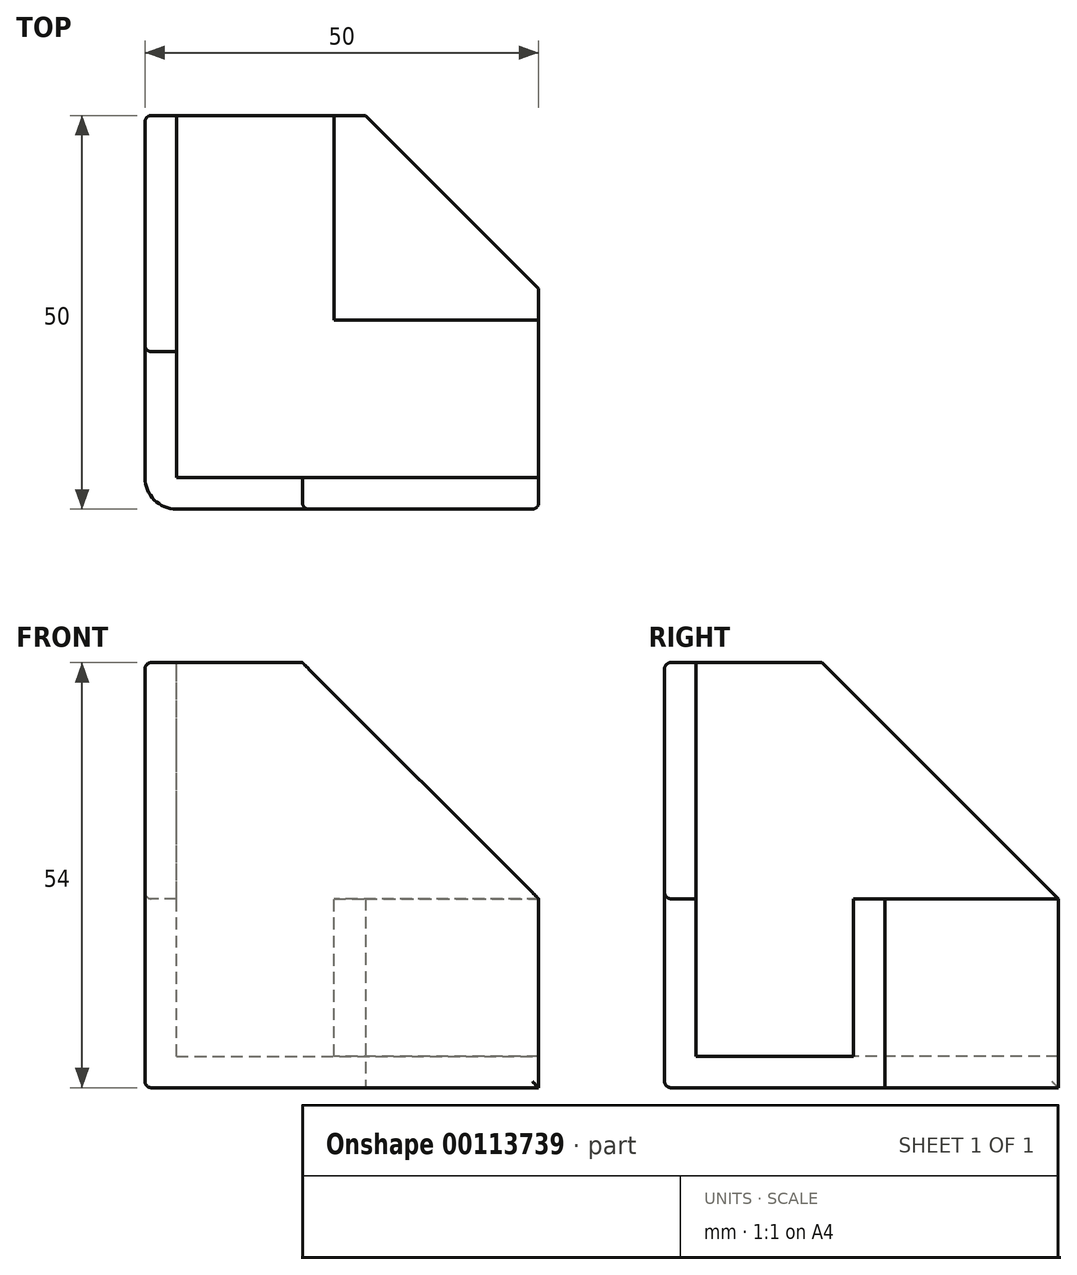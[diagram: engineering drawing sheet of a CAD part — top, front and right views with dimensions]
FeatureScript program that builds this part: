
annotation { "Feature Type Name" : "Feature", "Feature Type Description" : "" }
export const myFeature = defineFeature(function(context is Context, id is Id, definition is map)
    precondition{}
    {
        {
            var Q0;
            Q0=qCreatedBy(makeId("Top.planeOp"),FACE);
            var sketch = newSketch(context, id + "F0", { "sketchPlane" : qUnion([Q0])});
            skLineSegment(sketch, "E0", {"start": v(-64, 35.12) * mm, "end": v(-36, 35.12) * mm});
            skLineSegment(sketch, "E1", {"start": v(-36, 35.12) * mm, "end": v(-14, 13.12) * mm});
            skLineSegment(sketch, "E2", {"start": v(-14, 13.12) * mm, "end": v(-14, -14.88) * mm});
            skLineSegment(sketch, "E3", {"start": v(-14, -14.88) * mm, "end": v(-64, -14.88) * mm});
            skLineSegment(sketch, "E4", {"start": v(-64, -14.88) * mm, "end": v(-64, 35.12) * mm});
            skSolve(sketch);
        }
        {
            var Q0;
            Q0=makeQuery(id+"F0.imprint","IMPRINT",FACE,{"disambiguationData":[TD([[makeQuery(id+"F0.imprint","IMPRINT",EDGE,{"derivedFrom":sQuery(id+"F0.wireOp",EDGE,"E0")}),-1.0]])]});
            extrude(context, id + "F1", {"entities" : qUnion([Q0]), "depth" : 24 * mm});
        }
        {
            var Q0;
            Q0=makeQuery(id+"F1.opExtrude","CAP_FACE",FACE,{"disambiguationData":[OSD([sQuery(id+"F0.wireOp",EDGE,"E0"),sQuery(id+"F0.wireOp",EDGE,"E1"),sQuery(id+"F0.wireOp",EDGE,"E2"),sQuery(id+"F0.wireOp",EDGE,"E3"),sQuery(id+"F0.wireOp",EDGE,"E4")])],"isStart":false});
            var sketch = newSketch(context, id + "F2", { "sketchPlane" : qUnion([Q0])});
            skLineSegment(sketch, "E5", {"start": v(-60, 35.12) * mm, "end": v(-60, -10.88) * mm});
            skLineSegment(sketch, "E6", {"start": v(-60, -10.88) * mm, "end": v(-14, -10.88) * mm});
            skLineSegment(sketch, "E7", {"start": v(-14, -10.88) * mm, "end": v(-14, 9.12) * mm});
            skLineSegment(sketch, "E8", {"start": v(-14, 9.12) * mm, "end": v(-40, 9.12) * mm});
            skLineSegment(sketch, "E9", {"start": v(-40, 9.12) * mm, "end": v(-40, 35.12) * mm});
            skLineSegment(sketch, "E10", {"start": v(-40, 35.12) * mm, "end": v(-60, 35.12) * mm});
            skSolve(sketch);
        }
        {
            var Q0;
            Q0=makeQuery(id+"F2.imprint","IMPRINT",FACE,{"disambiguationData":[TD([[makeQuery(id+"F2.imprint","IMPRINT",EDGE,{"derivedFrom":sQuery(id+"F2.wireOp",EDGE,"E5")}),1.0]])]});
            extrude(context, id + "F3", {"entities" : qUnion([Q0]), "operationType" : NewBodyOperationType.REMOVE, "oppositeDirection" : true, "depth" : 20 * mm});
        }
        {
            var Q0;
            {var subQ0=sQuery(id+"F0.wireOp",EDGE,"E4");var subQ1=sQuery(id+"F0.wireOp",EDGE,"E3");var subQ2=sQuery(id+"F0.wireOp",EDGE,"E2");var subQ3=sQuery(id+"F0.wireOp",EDGE,"E0");Q0=makeQuery(id+"F3.boolean.opBoolean","SPLIT",FACE,{"disambiguationData":[TD([makeQuery(id+"F1.opExtrude","SWEPT_FACE",FACE,{"disambiguationData":[OSD([subQ1])]})])],"derivedFrom":makeQuery(id+"F1.opExtrude","CAP_FACE",FACE,{"disambiguationData":[OSD([subQ3,sQuery(id+"F0.wireOp",EDGE,"E1"),subQ2,subQ1,subQ0])],"isStart":false})});}
            extrude(context, id + "F4", {"entities" : qUnion([Q0]), "operationType" : NewBodyOperationType.ADD, "depth" : 30 * mm});
        }
        {
            var Q0;
            {var subQ0=sQuery(id+"F0.wireOp",EDGE,"E3");Q0=makeQuery(id+"F4.boolean.opBoolean","MERGE",FACE,{"derivedFrom":[makeQuery(id+"F1.opExtrude","SWEPT_FACE",FACE,{"disambiguationData":[OSD([subQ0])]}),makeQuery(id+"F4.opExtrude","SWEPT_FACE",FACE,{"disambiguationData":[OSD([subQ0])]})]});}
            var sketch = newSketch(context, id + "F5", { "sketchPlane" : qUnion([Q0])});
            skLineSegment(sketch, "E11", {"start": v(-14, 54) * mm, "end": v(-14, 24) * mm});
            skLineSegment(sketch, "E12", {"start": v(-14, 24) * mm, "end": v(-44, 54) * mm});
            skLineSegment(sketch, "E13", {"start": v(-44, 54) * mm, "end": v(-14, 54) * mm});
            skSolve(sketch);
        }
        {
            var Q0;
            Q0=makeQuery(id+"F5.imprint","IMPRINT",FACE,{"disambiguationData":[TD([[makeQuery(id+"F5.imprint","IMPRINT",EDGE,{"derivedFrom":sQuery(id+"F5.wireOp",EDGE,"E11")}),-1.0]])]});
            extrude(context, id + "F6", {"entities" : qUnion([Q0]), "operationType" : NewBodyOperationType.REMOVE, "oppositeDirection" : true, "depth" : 25 * mm});
        }
        {
            var Q0;
            {var subQ0=sQuery(id+"F0.wireOp",EDGE,"E4");Q0=makeQuery(id+"F4.boolean.opBoolean","MERGE",FACE,{"derivedFrom":[makeQuery(id+"F1.opExtrude","SWEPT_FACE",FACE,{"disambiguationData":[OSD([subQ0])]}),makeQuery(id+"F4.opExtrude","SWEPT_FACE",FACE,{"disambiguationData":[OSD([subQ0])]})]});}
            var sketch = newSketch(context, id + "F7", { "sketchPlane" : qUnion([Q0])});
            skLineSegment(sketch, "E14", {"start": v(-35.12, 54) * mm, "end": v(-35.12, 24) * mm});
            skLineSegment(sketch, "E15", {"start": v(-35.12, 24) * mm, "end": v(-5.12, 54) * mm});
            skLineSegment(sketch, "E16", {"start": v(-5.12, 54) * mm, "end": v(-35.12, 54) * mm});
            skSolve(sketch);
        }
        {
            var Q0;
            Q0=makeQuery(id+"F7.imprint","IMPRINT",FACE,{"disambiguationData":[TD([[makeQuery(id+"F7.imprint","IMPRINT",EDGE,{"derivedFrom":sQuery(id+"F7.wireOp",EDGE,"E14")}),1.0]])]});
            extrude(context, id + "F8", {"entities" : qUnion([Q0]), "operationType" : NewBodyOperationType.REMOVE, "oppositeDirection" : true, "depth" : 25 * mm});
        }
        {
            var Q0;
            Q0=makeQuery(id+"F4.opExtrude","CAP_EDGE",EDGE,{"disambiguationData":[OSD([sQuery(id+"F0.wireOp",EDGE,"E4")])],"isStart":false});
            var Q1;
            Q1=makeQuery(id+"F4.opExtrude","CAP_EDGE",EDGE,{"disambiguationData":[OSD([sQuery(id+"F0.wireOp",EDGE,"E3")])],"isStart":false});
            var Q2;
            Q2=makeQuery(id+"F8.boolean.opBoolean","COPY",EDGE,{"derivedFrom":makeQuery(id+"F8.opExtrude","CAP_EDGE",EDGE,{"disambiguationData":[OSD([sQuery(id+"F7.wireOp",EDGE,"E15")])],"isStart":true})});
            var Q3;
            Q3=makeQuery(id+"F6.boolean.opBoolean","COPY",EDGE,{"derivedFrom":makeQuery(id+"F6.opExtrude","CAP_EDGE",EDGE,{"disambiguationData":[OSD([sQuery(id+"F5.wireOp",EDGE,"E12")])],"isStart":true})});
            var Q4;
            {var subQ0=sQuery(id+"F0.wireOp",EDGE,"E4");var subQ1=sQuery(id+"F0.wireOp",EDGE,"E0");Q4=makeQuery(id+"F4.boolean.opBoolean","MERGE",EDGE,{"derivedFrom":[makeQuery(id+"F1.opExtrude","SWEPT_EDGE",EDGE,{"disambiguationData":[OSD([subQ1,subQ0])]}),makeQuery(id+"F4.opExtrude","SWEPT_EDGE",EDGE,{"disambiguationData":[OSD([subQ1,subQ0])]})]});}
            var Q5;
            {var subQ0=sQuery(id+"F0.wireOp",EDGE,"E3");var subQ1=sQuery(id+"F0.wireOp",EDGE,"E2");Q5=makeQuery(id+"F4.boolean.opBoolean","MERGE",EDGE,{"derivedFrom":[makeQuery(id+"F1.opExtrude","SWEPT_EDGE",EDGE,{"disambiguationData":[OSD([subQ1,subQ0])]}),makeQuery(id+"F4.opExtrude","SWEPT_EDGE",EDGE,{"disambiguationData":[OSD([subQ1,subQ0])]})]});}
            var Q6;
            Q6=makeQuery(id+"F1.opExtrude","CAP_EDGE",EDGE,{"disambiguationData":[OSD([sQuery(id+"F0.wireOp",EDGE,"E4")])],"isStart":true});
            var Q7;
            Q7=makeQuery(id+"F1.opExtrude","CAP_EDGE",EDGE,{"disambiguationData":[OSD([sQuery(id+"F0.wireOp",EDGE,"E3")])],"isStart":true});
            fillet(context, id + "F9", {"entities" : qUnion([Q0, Q1, Q2, Q3, Q4, Q5, Q6, Q7]), "radius" : 0.8 * mm, "tangentPropagation" : true, "allowEdgeOverflow" : false});
        }
        {
            var Q0;
            {var subQ0=sQuery(id+"F0.wireOp",EDGE,"E4");var subQ1=sQuery(id+"F0.wireOp",EDGE,"E3");Q0=makeQuery(id+"F4.boolean.opBoolean","MERGE",EDGE,{"derivedFrom":[makeQuery(id+"F1.opExtrude","SWEPT_EDGE",EDGE,{"disambiguationData":[OSD([subQ1,subQ0])]}),makeQuery(id+"F4.opExtrude","SWEPT_EDGE",EDGE,{"disambiguationData":[OSD([subQ1,subQ0])]})]});}
            fillet(context, id + "F10", {"entities" : qUnion([Q0]), "radius" : 4 * mm, "tangentPropagation" : true, "allowEdgeOverflow" : false});
        }
    });
